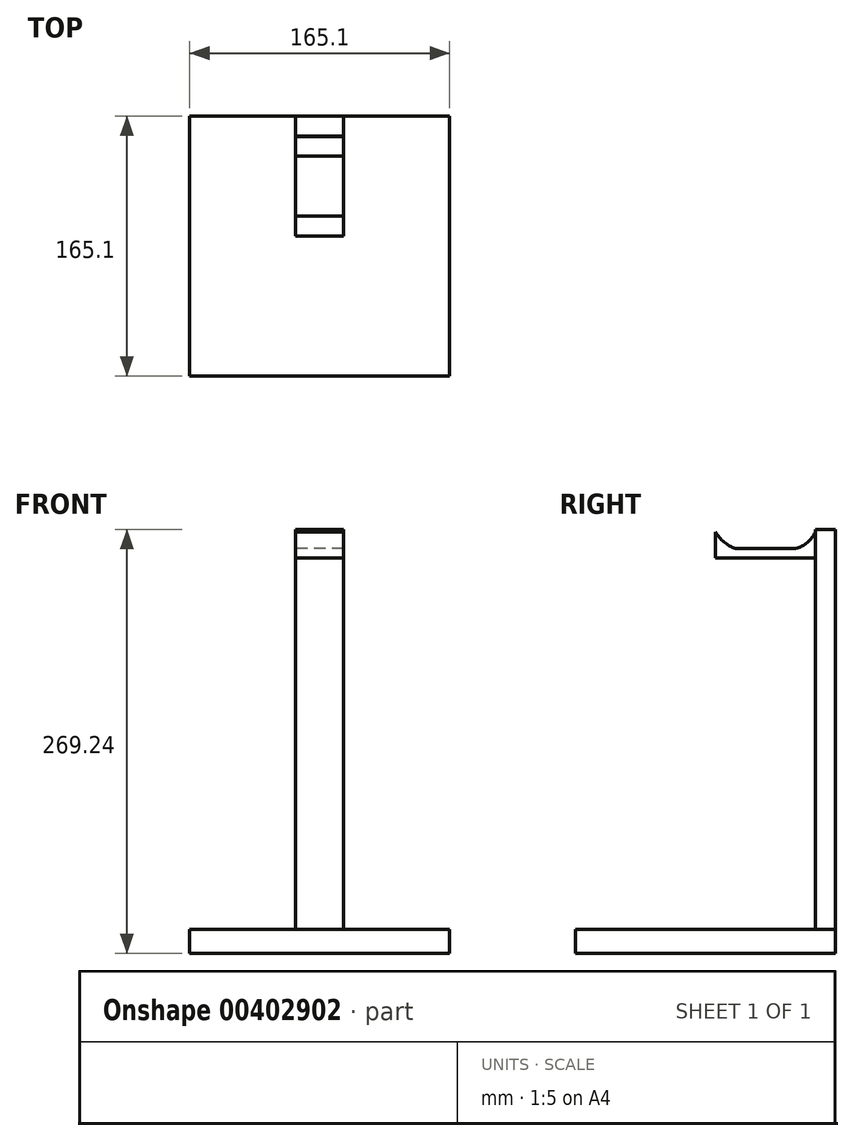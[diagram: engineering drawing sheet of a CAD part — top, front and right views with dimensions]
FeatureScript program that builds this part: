
annotation { "Feature Type Name" : "Feature", "Feature Type Description" : "" }
export const myFeature = defineFeature(function(context is Context, id is Id, definition is map)
    precondition{}
    {
        {
            var Q0;
            Q0=qCreatedBy(makeId("Front.planeOp"),FACE);
            var sketch = newSketch(context, id + "F0", { "sketchPlane" : qUnion([Q0])});
            skLineSegment(sketch, "E0.bottom", {"start": v(82.55, 7.62) * mm, "end": v(-82.55, 7.62) * mm});
            skLineSegment(sketch, "E0.top", {"start": v(82.55, -7.62) * mm, "end": v(-82.55, -7.62) * mm});
            skLineSegment(sketch, "E0.left", {"start": v(82.55, 7.62) * mm, "end": v(82.55, -7.62) * mm});
            skLineSegment(sketch, "E0.right", {"start": v(-82.55, 7.62) * mm, "end": v(-82.55, -7.62) * mm});
            skPoint(sketch, "E0.middle", {"position": v(0, 0) * mm});
            skSolve(sketch);
        }
        {
            var Q0;
            Q0=qSketchRegion(id+"F0",true);
            extrude(context, id + "F1", {"entities" : qUnion([Q0]), "endBound" : BoundingType.SYMMETRIC, "oppositeDirection" : true, "depth" : 165.1 * mm});
        }
        {
            var Q0;
            Q0=makeQuery(id+"F1.opExtrude","SWEPT_FACE",FACE,{"disambiguationData":[OSD([sQuery(id+"F0.wireOp",EDGE,"E0.bottom")])]});
            var sketch = newSketch(context, id + "F2", { "sketchPlane" : qUnion([Q0])});
            skLineSegment(sketch, "E1.bottom", {"start": v(-15.24, 82.55) * mm, "end": v(15.24, 82.55) * mm});
            skLineSegment(sketch, "E1.top", {"start": v(-15.24, 69.85) * mm, "end": v(15.24, 69.85) * mm});
            skLineSegment(sketch, "E1.left", {"start": v(-15.24, 82.55) * mm, "end": v(-15.24, 69.85) * mm});
            skLineSegment(sketch, "E1.right", {"start": v(15.24, 82.55) * mm, "end": v(15.24, 69.85) * mm});
            skLineSegment(sketch, "E2.bottom", {"start": v(-38.1, 0) * mm, "end": v(-12.7, 0) * mm});
            skLineSegment(sketch, "E2.top", {"start": v(-38.1, -17.78) * mm, "end": v(-12.7, -17.78) * mm});
            skLineSegment(sketch, "E2.left", {"start": v(-38.1, 0) * mm, "end": v(-38.1, -17.78) * mm});
            skLineSegment(sketch, "E2.right", {"start": v(-12.7, 0) * mm, "end": v(-12.7, -17.78) * mm});
            skLineSegment(sketch, "E3.bottom", {"start": v(12.7, 0) * mm, "end": v(38.1, 0) * mm});
            skLineSegment(sketch, "E3.top", {"start": v(12.7, -17.78) * mm, "end": v(38.1, -17.78) * mm});
            skLineSegment(sketch, "E3.left", {"start": v(12.7, 0) * mm, "end": v(12.7, -17.78) * mm});
            skLineSegment(sketch, "E3.right", {"start": v(38.1, 0) * mm, "end": v(38.1, -17.78) * mm});
            skArc(sketch, "E4", {"start": v(-12.7, -17.78) * mm, "mid": v(-20.14, -35.74) * mm, "end": v(-38.1, -43.18) * mm});
            skLineSegment(sketch, "E5", {"start": v(-38.1, -17.78) * mm, "end": v(-38.1, -43.18) * mm});
            skArc(sketch, "E6", {"start": v(12.7, -17.78) * mm, "mid": v(20.14, -35.74) * mm, "end": v(38.1, -43.18) * mm});
            skLineSegment(sketch, "E7", {"start": v(38.1, -17.78) * mm, "end": v(38.1, -43.18) * mm});
            skLineSegment(sketch, "E8", {"start": v(38.1, 0) * mm, "end": v(38.1, 21.23) * mm});
            skLineSegment(sketch, "E9", {"start": v(-38.1, 0) * mm, "end": v(-38.1, 21.23) * mm});
            skFitSpline(sketch, "E10", {"points": [v(-12.7, 0) * mm, v(-38.1, 21.23) * mm], "startDerivative": vector(-38.1, 0) * mm, "endDerivative": vector(0, 63.68) * mm});
            skFitSpline(sketch, "E11", {"points": [v(38.1, 21.23) * mm, v(12.7, 0) * mm], "startDerivative": vector(0, -63.68) * mm, "endDerivative": vector(-27.64, 0) * mm});
            skLineSegment(sketch, "E12", {"start": v(-10.78, 17.94) * mm, "end": v(0, 7.17) * mm});
            skLineSegment(sketch, "E13", {"start": v(0, 7.17) * mm, "end": v(10.78, 17.94) * mm});
            skLineSegment(sketch, "E14", {"start": v(-10.78, 17.94) * mm, "end": v(10.78, 17.94) * mm});
            skCircle(sketch, "E15", {"center": v(25.2, 32.37) * mm, "radius": 6.35 * mm});
            skCircle(sketch, "E16", {"center": v(-25.2, 32.37) * mm, "radius": 6.35 * mm});
            skPoint(sketch, "E17", {"position": v(0, 17.94) * mm});
            skPoint(sketch, "E18", {"position": v(38.1, 51.82) * mm});
            skPoint(sketch, "E19", {"position": v(-38.1, 51.82) * mm});
            skFitSpline(sketch, "E20", {"points": [v(0, 17.94) * mm, v(-38.1, 51.82) * mm], "startDerivative": vector(0, 62.62) * mm, "endDerivative": vector(-84.2, 0) * mm});
            skFitSpline(sketch, "E21", {"points": [v(0, 17.94) * mm, v(38.1, 51.82) * mm], "startDerivative": vector(0, 62.62) * mm, "endDerivative": vector(80.13, 0) * mm});
            skArc(sketch, "E22", {"start": v(38.1, 51.82) * mm, "mid": v(0, 60.9) * mm, "end": v(-38.1, 51.82) * mm});
            skSolve(sketch);
        }
        {
            var Q0;
            Q0=makeQuery(id+"F2.imprint","IMPRINT",FACE,{"disambiguationData":[TD([[makeQuery(id+"F2.imprint","IMPRINT",EDGE,{"derivedFrom":sQuery(id+"F2.wireOp",EDGE,"E1.bottom")}),1.0]])]});
            extrude(context, id + "F3", {"entities" : qUnion([Q0]), "operationType" : NewBodyOperationType.ADD, "depth" : 254 * mm});
        }
        {
            var Q0;
            Q0=qCreatedBy(makeId("Right.planeOp"),FACE);
            var sketch = newSketch(context, id + "F4", { "sketchPlane" : qUnion([Q0])});
            skLineSegment(sketch, "E23.bottom", {"start": v(69.82, 249.55) * mm, "end": v(6.32, 249.55) * mm});
            skLineSegment(sketch, "E23.top", {"start": v(69.82, 243.6) * mm, "end": v(6.32, 243.6) * mm});
            skLineSegment(sketch, "E23.left", {"start": v(69.82, 249.55) * mm, "end": v(69.82, 243.6) * mm});
            skLineSegment(sketch, "E23.right", {"start": v(6.32, 249.55) * mm, "end": v(6.32, 243.6) * mm});
            skPoint(sketch, "E24", {"position": v(69.67, 260.1) * mm});
            skLineSegment(sketch, "E25", {"start": v(6.32, 249.55) * mm, "end": v(6.32, 260.1) * mm});
            skPoint(sketch, "E26", {"position": v(19.02, 249.55) * mm});
            skPoint(sketch, "E27", {"position": v(57.12, 249.55) * mm});
            skArc(sketch, "E28", {"start": v(57.12, 249.55) * mm, "mid": v(64.62, 253.37) * mm, "end": v(69.67, 260.1) * mm});
            skArc(sketch, "E29", {"start": v(6.32, 260.1) * mm, "mid": v(11.7, 253.65) * mm, "end": v(19.02, 249.55) * mm});
            skLineSegment(sketch, "E30", {"start": v(69.67, 260.1) * mm, "end": v(69.82, 249.55) * mm});
            skSolve(sketch);
        }
        {
            var Q0;
            Q0=qSketchRegion(id+"F4",true);
            extrude(context, id + "F5", {"entities" : qUnion([Q0]), "endBound" : BoundingType.SYMMETRIC, "depth" : 30.48 * mm});
        }
    });
